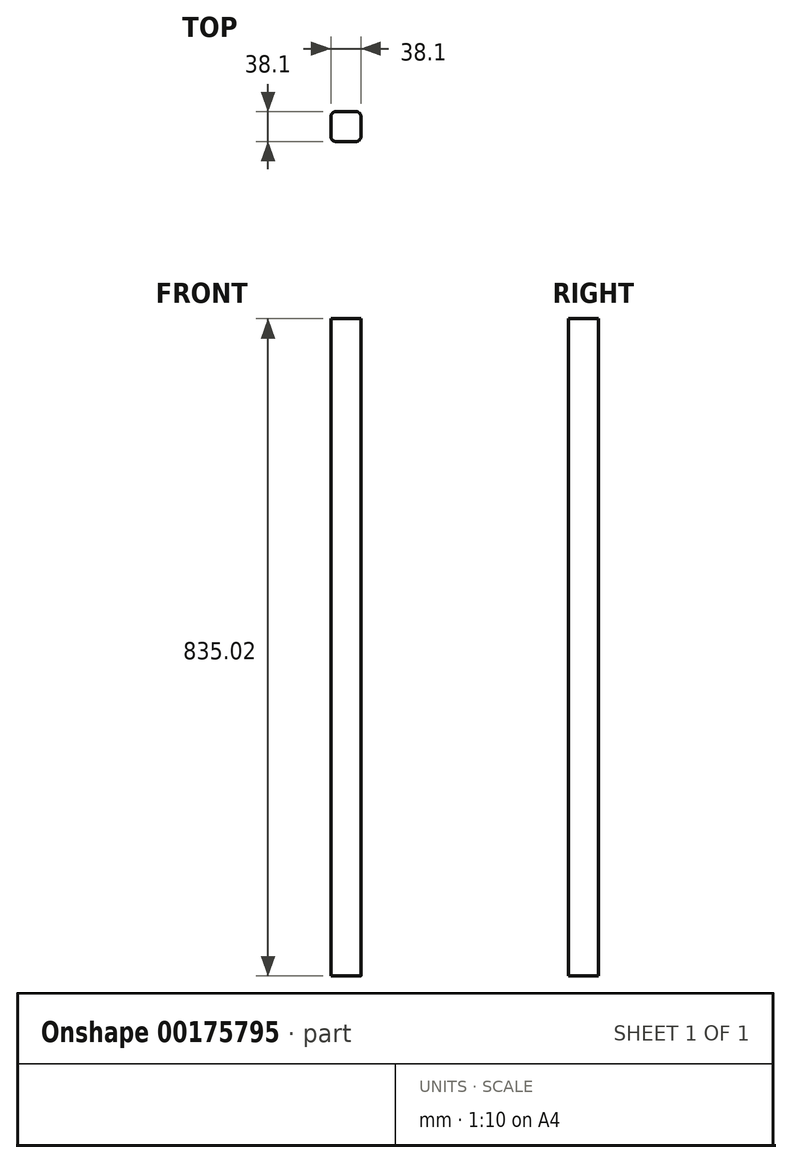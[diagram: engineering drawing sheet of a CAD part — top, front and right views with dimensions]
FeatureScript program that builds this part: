
annotation { "Feature Type Name" : "Feature", "Feature Type Description" : "" }
export const myFeature = defineFeature(function(context is Context, id is Id, definition is map)
    precondition{}
    {
        {
            var Q0;
            Q0=qCreatedBy(makeId("Top.planeOp"),FACE);
            var sketch = newSketch(context, id + "F0", { "sketchPlane" : qUnion([Q0])});
            skLineSegment(sketch, "E0.bottom", {"start": v(12.7, 19.05) * mm, "end": v(-12.7, 19.05) * mm});
            skLineSegment(sketch, "E0.top", {"start": v(12.7, -19.05) * mm, "end": v(-12.7, -19.05) * mm});
            skLineSegment(sketch, "E0.left", {"start": v(19.05, 12.7) * mm, "end": v(19.05, -12.7) * mm});
            skLineSegment(sketch, "E0.right", {"start": v(-19.05, 12.7) * mm, "end": v(-19.05, -12.7) * mm});
            skPoint(sketch, "E0.middle", {"position": v(0, 0) * mm});
            skPoint(sketch, "E1.visualSharp", {"position": v(-19.05, 19.05) * mm});
            skArc(sketch, "E1.filletArc", {"start": v(-12.7, 19.05) * mm, "mid": v(-17.2, 17.2) * mm, "end": v(-19.05, 12.7) * mm});
            skPoint(sketch, "E2.visualSharp", {"position": v(19.05, 19.05) * mm});
            skArc(sketch, "E2.filletArc", {"start": v(19.05, 12.7) * mm, "mid": v(17.2, 17.2) * mm, "end": v(12.7, 19.05) * mm});
            skPoint(sketch, "E3.visualSharp", {"position": v(19.05, -19.05) * mm});
            skArc(sketch, "E3.filletArc", {"start": v(12.7, -19.05) * mm, "mid": v(17.2, -17.2) * mm, "end": v(19.05, -12.7) * mm});
            skPoint(sketch, "E4.visualSharp", {"position": v(-19.05, -19.05) * mm});
            skArc(sketch, "E4.filletArc", {"start": v(-19.05, -12.7) * mm, "mid": v(-17.2, -17.2) * mm, "end": v(-12.7, -19.05) * mm});
            skSolve(sketch);
        }
        {
            var Q0;
            Q0=qSketchRegion(id+"F0",true);
            extrude(context, id + "F1", {"entities" : qUnion([Q0]), "depth" : 835.02 * mm, "offsetDistance" : 25.4 * mm});
        }
    });
